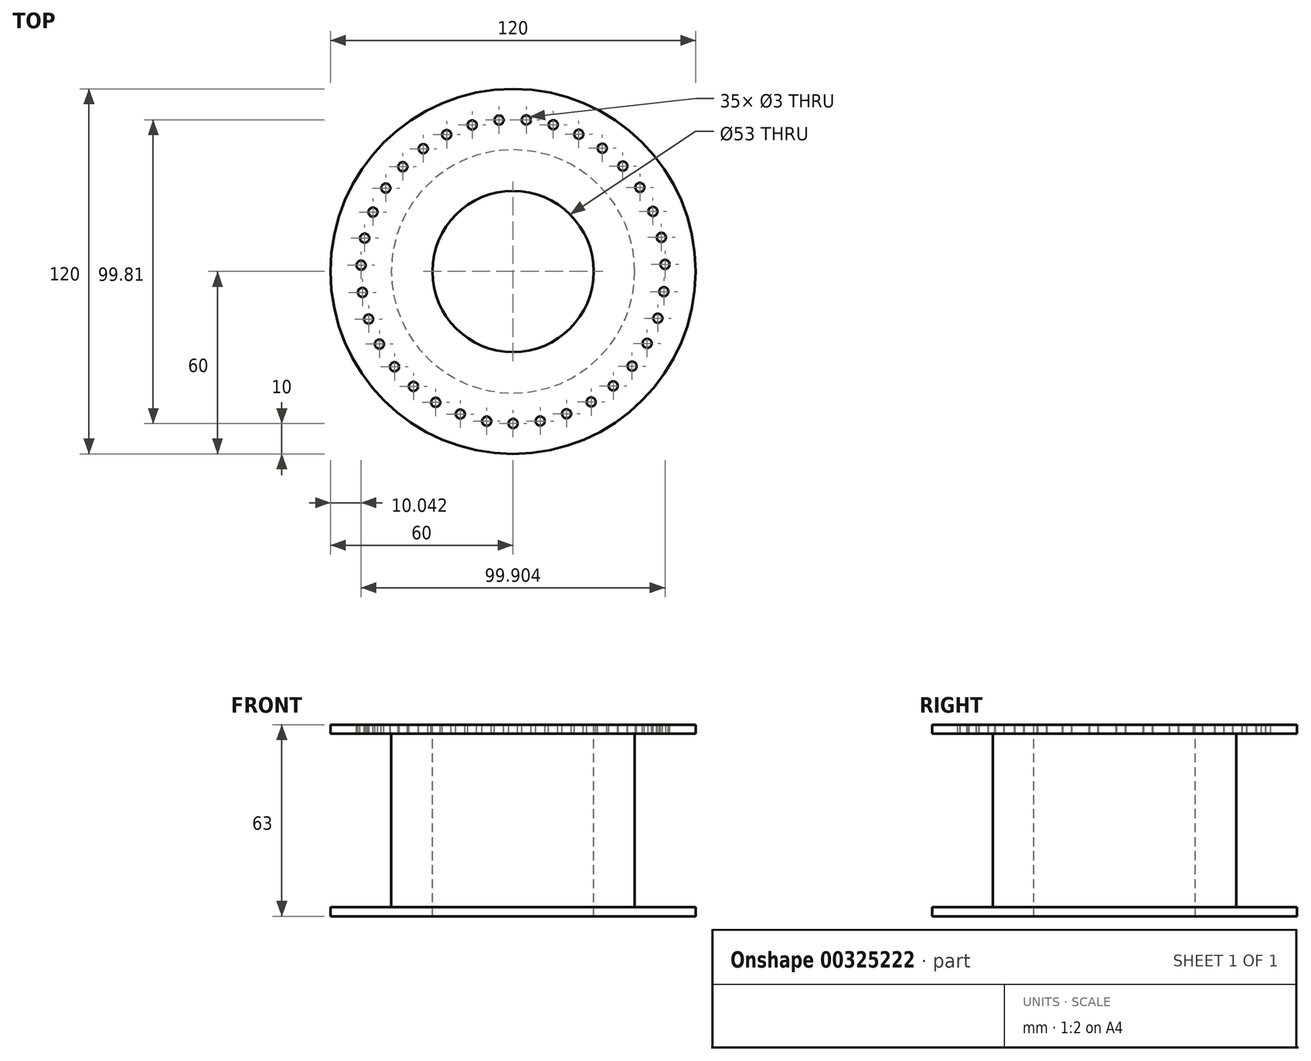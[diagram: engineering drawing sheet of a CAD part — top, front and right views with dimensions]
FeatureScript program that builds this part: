
annotation { "Feature Type Name" : "Feature", "Feature Type Description" : "" }
export const myFeature = defineFeature(function(context is Context, id is Id, definition is map)
    precondition{}
    {
        {
            var Q0;
            Q0=qCreatedBy(makeId("Top.planeOp"),FACE);
            var sketch = newSketch(context, id + "F0", { "sketchPlane" : qUnion([Q0])});
            skCircle(sketch, "E0", {"center": v(0, 0) * mm, "radius": 60 * mm});
            skSolve(sketch);
        }
        {
            var Q0;
            Q0=makeQuery(id+"F0.imprint","IMPRINT",FACE,{"disambiguationData":[TD([[makeQuery(id+"F0.imprint","IMPRINT",EDGE,{"derivedFrom":sQuery(id+"F0.wireOp",EDGE,"E0")}),1.0]])]});
            extrude(context, id + "F1", {"entities" : qUnion([Q0]), "depth" : 3 * mm});
        }
        {
            var Q0;
            Q0=makeQuery(id+"F1.opExtrude","CAP_FACE",FACE,{"disambiguationData":[OSD([sQuery(id+"F0.wireOp",EDGE,"E0")])],"isStart":false});
            var sketch = newSketch(context, id + "F2", { "sketchPlane" : qUnion([Q0])});
            skCircle(sketch, "E1", {"center": v(0, 0) * mm, "radius": 40 * mm});
            skSolve(sketch);
        }
        {
            var Q0;
            Q0=makeQuery(id+"F2.imprint","IMPRINT",FACE,{"disambiguationData":[TD([[makeQuery(id+"F2.imprint","IMPRINT",EDGE,{"derivedFrom":sQuery(id+"F2.wireOp",EDGE,"E1")}),1.0]])]});
            extrude(context, id + "F3", {"entities" : qUnion([Q0]), "operationType" : NewBodyOperationType.ADD, "depth" : 57 * mm});
        }
        {
            var Q0;
            Q0=makeQuery(id+"F3.opExtrude","CAP_FACE",FACE,{"disambiguationData":[OSD([sQuery(id+"F2.wireOp",EDGE,"E1")])],"isStart":false});
            var sketch = newSketch(context, id + "F4", { "sketchPlane" : qUnion([Q0])});
            skCircle(sketch, "E2", {"center": v(0, 0) * mm, "radius": 60 * mm});
            skSolve(sketch);
        }
        {
            var Q0;
            Q0=makeQuery(id+"F4.imprint","IMPRINT",FACE,{"disambiguationData":[TD([[makeQuery(id+"F4.imprint","IMPRINT",EDGE,{"derivedFrom":sQuery(id+"F4.wireOp",EDGE,"E2")}),1.0]])]});
            var Q1;
            Q1=makeQuery(id+"F4.imprint","IMPRINT",FACE,{"disambiguationData":[TD([[makeQuery(id+"F4.imprint","IMPRINT",EDGE,{"derivedFrom":makeQuery(id+"F3.opExtrude","CAP_EDGE",EDGE,{"disambiguationData":[OSD([sQuery(id+"F2.wireOp",EDGE,"E1")])],"isStart":false})}),1.0]])]});
            extrude(context, id + "F5", {"entities" : qUnion([Q0, Q1]), "operationType" : NewBodyOperationType.ADD, "depth" : 3 * mm});
        }
        {
            var Q0;
            Q0=makeQuery(id+"F5.opExtrude","CAP_FACE",FACE,{"disambiguationData":[OSD([sQuery(id+"F4.wireOp",EDGE,"E2")])],"isStart":false});
            var sketch = newSketch(context, id + "F6", { "sketchPlane" : qUnion([Q0])});
            skCircle(sketch, "E3", {"center": v(0, 0) * mm, "radius": 26.5 * mm});
            skSolve(sketch);
        }
        {
            var Q0;
            Q0=makeQuery(id+"F6.imprint","IMPRINT",FACE,{"disambiguationData":[TD([[makeQuery(id+"F6.imprint","IMPRINT",EDGE,{"derivedFrom":sQuery(id+"F6.wireOp",EDGE,"E3")}),1.0]])]});
            extrude(context, id + "F7", {"entities" : qUnion([Q0]), "operationType" : NewBodyOperationType.REMOVE, "oppositeDirection" : true, "depth" : 63 * mm});
        }
        {
            var Q0;
            Q0=makeQuery(id+"F5.opExtrude","CAP_FACE",FACE,{"disambiguationData":[OSD([sQuery(id+"F4.wireOp",EDGE,"E2")])],"isStart":false});
            var sketch = newSketch(context, id + "F8", { "sketchPlane" : qUnion([Q0])});
            skCircle(sketch, "E4", {"center": v(0, -50) * mm, "radius": 1.5 * mm});
            skCircle(sketch, "E5.1.0", {"center": v(8.94, -49.2) * mm, "radius": 1.5 * mm});
            skCircle(sketch, "E5.2.0", {"center": v(17.58, -46.8) * mm, "radius": 1.5 * mm});
            skCircle(sketch, "E5.3.0", {"center": v(25.66, -42.91) * mm, "radius": 1.5 * mm});
            skCircle(sketch, "E5.4.0", {"center": v(32.92, -37.63) * mm, "radius": 1.5 * mm});
            skCircle(sketch, "E5.5.0", {"center": v(39.11, -31.15) * mm, "radius": 1.5 * mm});
            skCircle(sketch, "E5.6.0", {"center": v(44.05, -23.65) * mm, "radius": 1.5 * mm});
            skCircle(sketch, "E5.7.0", {"center": v(47.57, -15.4) * mm, "radius": 1.5 * mm});
            skCircle(sketch, "E5.8.0", {"center": v(49.56, -6.65) * mm, "radius": 1.5 * mm});
            skCircle(sketch, "E5.9.0", {"center": v(49.95, 2.3) * mm, "radius": 1.5 * mm});
            skCircle(sketch, "E5.10.0", {"center": v(48.73, 11.2) * mm, "radius": 1.5 * mm});
            skCircle(sketch, "E5.11.0", {"center": v(45.94, 19.73) * mm, "radius": 1.5 * mm});
            skCircle(sketch, "E5.12.0", {"center": v(41.68, 27.62) * mm, "radius": 1.5 * mm});
            skCircle(sketch, "E5.13.0", {"center": v(36.07, 34.62) * mm, "radius": 1.5 * mm});
            skCircle(sketch, "E5.14.0", {"center": v(29.3, 40.51) * mm, "radius": 1.5 * mm});
            skCircle(sketch, "E5.15.0", {"center": v(21.6, 45.1) * mm, "radius": 1.5 * mm});
            skCircle(sketch, "E5.16.0", {"center": v(13.19, 48.23) * mm, "radius": 1.5 * mm});
            skCircle(sketch, "E5.17.0", {"center": v(4.36, 49.8) * mm, "radius": 1.5 * mm});
            skCircle(sketch, "E5.18.0", {"center": v(-4.61, 49.79) * mm, "radius": 1.5 * mm});
            skCircle(sketch, "E5.19.0", {"center": v(-13.44, 48.16) * mm, "radius": 1.5 * mm});
            skCircle(sketch, "E5.20.0", {"center": v(-21.83, 44.98) * mm, "radius": 1.5 * mm});
            skCircle(sketch, "E5.21.0", {"center": v(-29.51, 40.36) * mm, "radius": 1.5 * mm});
            skCircle(sketch, "E5.22.0", {"center": v(-36.25, 34.44) * mm, "radius": 1.5 * mm});
            skCircle(sketch, "E5.23.0", {"center": v(-41.82, 27.4) * mm, "radius": 1.5 * mm});
            skCircle(sketch, "E5.24.0", {"center": v(-46.05, 19.49) * mm, "radius": 1.5 * mm});
            skCircle(sketch, "E5.25.0", {"center": v(-48.79, 10.95) * mm, "radius": 1.5 * mm});
            skCircle(sketch, "E5.26.0", {"center": v(-49.96, 2.05) * mm, "radius": 1.5 * mm});
            skCircle(sketch, "E5.27.0", {"center": v(-49.52, -6.9) * mm, "radius": 1.5 * mm});
            skCircle(sketch, "E5.28.0", {"center": v(-47.49, -15.65) * mm, "radius": 1.5 * mm});
            skCircle(sketch, "E5.29.0", {"center": v(-43.93, -23.88) * mm, "radius": 1.5 * mm});
            skCircle(sketch, "E5.30.0", {"center": v(-38.95, -31.35) * mm, "radius": 1.5 * mm});
            skCircle(sketch, "E5.31.0", {"center": v(-32.73, -37.8) * mm, "radius": 1.5 * mm});
            skCircle(sketch, "E5.32.0", {"center": v(-25.44, -43.04) * mm, "radius": 1.5 * mm});
            skCircle(sketch, "E5.33.0", {"center": v(-17.34, -46.9) * mm, "radius": 1.5 * mm});
            skCircle(sketch, "E5.34.0", {"center": v(-8.68, -49.24) * mm, "radius": 1.5 * mm});
            skPoint(sketch, "E5.center", {"position": v(0, 0) * mm});
            skLineSegment(sketch, "E5.anchor1", {"start": v(0, 0) * mm, "end": v(0, -50) * mm, "construction": true});
            skLineSegment(sketch, "E5.anchor2", {"start": v(0, 0) * mm, "end": v(-8.68, -49.24) * mm, "construction": true});
            skSolve(sketch);
        }
        {
            var Q0;
            Q0=makeQuery(id+"F8.imprint","IMPRINT",FACE,{"disambiguationData":[TD([[makeQuery(id+"F8.imprint","IMPRINT",EDGE,{"derivedFrom":sQuery(id+"F8.wireOp",EDGE,"E5.27.0")}),1.0]])]});
            var Q1;
            Q1=makeQuery(id+"F8.imprint","IMPRINT",FACE,{"disambiguationData":[TD([[makeQuery(id+"F8.imprint","IMPRINT",EDGE,{"derivedFrom":sQuery(id+"F8.wireOp",EDGE,"E5.26.0")}),1.0]])]});
            var Q2;
            Q2=makeQuery(id+"F8.imprint","IMPRINT",FACE,{"disambiguationData":[TD([[makeQuery(id+"F8.imprint","IMPRINT",EDGE,{"derivedFrom":sQuery(id+"F8.wireOp",EDGE,"E5.25.0")}),1.0]])]});
            var Q3;
            Q3=makeQuery(id+"F8.imprint","IMPRINT",FACE,{"disambiguationData":[TD([[makeQuery(id+"F8.imprint","IMPRINT",EDGE,{"derivedFrom":sQuery(id+"F8.wireOp",EDGE,"E5.28.0")}),1.0]])]});
            var Q4;
            Q4=makeQuery(id+"F8.imprint","IMPRINT",FACE,{"disambiguationData":[TD([[makeQuery(id+"F8.imprint","IMPRINT",EDGE,{"derivedFrom":sQuery(id+"F8.wireOp",EDGE,"E5.29.0")}),1.0]])]});
            var Q5;
            Q5=makeQuery(id+"F8.imprint","IMPRINT",FACE,{"disambiguationData":[TD([[makeQuery(id+"F8.imprint","IMPRINT",EDGE,{"derivedFrom":sQuery(id+"F8.wireOp",EDGE,"E5.30.0")}),1.0]])]});
            var Q6;
            Q6=makeQuery(id+"F8.imprint","IMPRINT",FACE,{"disambiguationData":[TD([[makeQuery(id+"F8.imprint","IMPRINT",EDGE,{"derivedFrom":sQuery(id+"F8.wireOp",EDGE,"E5.31.0")}),1.0]])]});
            var Q7;
            Q7=makeQuery(id+"F8.imprint","IMPRINT",FACE,{"disambiguationData":[TD([[makeQuery(id+"F8.imprint","IMPRINT",EDGE,{"derivedFrom":sQuery(id+"F8.wireOp",EDGE,"E5.32.0")}),1.0]])]});
            var Q8;
            Q8=makeQuery(id+"F8.imprint","IMPRINT",FACE,{"disambiguationData":[TD([[makeQuery(id+"F8.imprint","IMPRINT",EDGE,{"derivedFrom":sQuery(id+"F8.wireOp",EDGE,"E5.33.0")}),1.0]])]});
            var Q9;
            Q9=makeQuery(id+"F8.imprint","IMPRINT",FACE,{"disambiguationData":[TD([[makeQuery(id+"F8.imprint","IMPRINT",EDGE,{"derivedFrom":sQuery(id+"F8.wireOp",EDGE,"E5.34.0")}),1.0]])]});
            var Q10;
            Q10=makeQuery(id+"F8.imprint","IMPRINT",FACE,{"disambiguationData":[TD([[makeQuery(id+"F8.imprint","IMPRINT",EDGE,{"derivedFrom":sQuery(id+"F8.wireOp",EDGE,"E4")}),1.0]])]});
            var Q11;
            Q11=makeQuery(id+"F8.imprint","IMPRINT",FACE,{"disambiguationData":[TD([[makeQuery(id+"F8.imprint","IMPRINT",EDGE,{"derivedFrom":sQuery(id+"F8.wireOp",EDGE,"E5.1.0")}),1.0]])]});
            var Q12;
            Q12=makeQuery(id+"F8.imprint","IMPRINT",FACE,{"disambiguationData":[TD([[makeQuery(id+"F8.imprint","IMPRINT",EDGE,{"derivedFrom":sQuery(id+"F8.wireOp",EDGE,"E5.2.0")}),1.0]])]});
            var Q13;
            Q13=makeQuery(id+"F8.imprint","IMPRINT",FACE,{"disambiguationData":[TD([[makeQuery(id+"F8.imprint","IMPRINT",EDGE,{"derivedFrom":sQuery(id+"F8.wireOp",EDGE,"E5.3.0")}),1.0]])]});
            var Q14;
            Q14=makeQuery(id+"F8.imprint","IMPRINT",FACE,{"disambiguationData":[TD([[makeQuery(id+"F8.imprint","IMPRINT",EDGE,{"derivedFrom":sQuery(id+"F8.wireOp",EDGE,"E5.4.0")}),1.0]])]});
            var Q15;
            Q15=makeQuery(id+"F8.imprint","IMPRINT",FACE,{"disambiguationData":[TD([[makeQuery(id+"F8.imprint","IMPRINT",EDGE,{"derivedFrom":sQuery(id+"F8.wireOp",EDGE,"E5.6.0")}),1.0]])]});
            var Q16;
            Q16=makeQuery(id+"F8.imprint","IMPRINT",FACE,{"disambiguationData":[TD([[makeQuery(id+"F8.imprint","IMPRINT",EDGE,{"derivedFrom":sQuery(id+"F8.wireOp",EDGE,"E5.7.0")}),1.0]])]});
            var Q17;
            Q17=makeQuery(id+"F8.imprint","IMPRINT",FACE,{"disambiguationData":[TD([[makeQuery(id+"F8.imprint","IMPRINT",EDGE,{"derivedFrom":sQuery(id+"F8.wireOp",EDGE,"E5.8.0")}),1.0]])]});
            var Q18;
            Q18=makeQuery(id+"F8.imprint","IMPRINT",FACE,{"disambiguationData":[TD([[makeQuery(id+"F8.imprint","IMPRINT",EDGE,{"derivedFrom":sQuery(id+"F8.wireOp",EDGE,"E5.5.0")}),1.0]])]});
            var Q19;
            Q19=makeQuery(id+"F8.imprint","IMPRINT",FACE,{"disambiguationData":[TD([[makeQuery(id+"F8.imprint","IMPRINT",EDGE,{"derivedFrom":sQuery(id+"F8.wireOp",EDGE,"E5.9.0")}),1.0]])]});
            var Q20;
            Q20=makeQuery(id+"F8.imprint","IMPRINT",FACE,{"disambiguationData":[TD([[makeQuery(id+"F8.imprint","IMPRINT",EDGE,{"derivedFrom":sQuery(id+"F8.wireOp",EDGE,"E5.10.0")}),1.0]])]});
            var Q21;
            Q21=makeQuery(id+"F8.imprint","IMPRINT",FACE,{"disambiguationData":[TD([[makeQuery(id+"F8.imprint","IMPRINT",EDGE,{"derivedFrom":sQuery(id+"F8.wireOp",EDGE,"E5.11.0")}),1.0]])]});
            var Q22;
            Q22=makeQuery(id+"F8.imprint","IMPRINT",FACE,{"disambiguationData":[TD([[makeQuery(id+"F8.imprint","IMPRINT",EDGE,{"derivedFrom":sQuery(id+"F8.wireOp",EDGE,"E5.12.0")}),1.0]])]});
            var Q23;
            Q23=makeQuery(id+"F8.imprint","IMPRINT",FACE,{"disambiguationData":[TD([[makeQuery(id+"F8.imprint","IMPRINT",EDGE,{"derivedFrom":sQuery(id+"F8.wireOp",EDGE,"E5.13.0")}),1.0]])]});
            var Q24;
            Q24=makeQuery(id+"F8.imprint","IMPRINT",FACE,{"disambiguationData":[TD([[makeQuery(id+"F8.imprint","IMPRINT",EDGE,{"derivedFrom":sQuery(id+"F8.wireOp",EDGE,"E5.15.0")}),1.0]])]});
            var Q25;
            Q25=makeQuery(id+"F8.imprint","IMPRINT",FACE,{"disambiguationData":[TD([[makeQuery(id+"F8.imprint","IMPRINT",EDGE,{"derivedFrom":sQuery(id+"F8.wireOp",EDGE,"E5.14.0")}),1.0]])]});
            var Q26;
            Q26=makeQuery(id+"F8.imprint","IMPRINT",FACE,{"disambiguationData":[TD([[makeQuery(id+"F8.imprint","IMPRINT",EDGE,{"derivedFrom":sQuery(id+"F8.wireOp",EDGE,"E5.16.0")}),1.0]])]});
            var Q27;
            Q27=makeQuery(id+"F8.imprint","IMPRINT",FACE,{"disambiguationData":[TD([[makeQuery(id+"F8.imprint","IMPRINT",EDGE,{"derivedFrom":sQuery(id+"F8.wireOp",EDGE,"E5.19.0")}),1.0]])]});
            var Q28;
            Q28=makeQuery(id+"F8.imprint","IMPRINT",FACE,{"disambiguationData":[TD([[makeQuery(id+"F8.imprint","IMPRINT",EDGE,{"derivedFrom":sQuery(id+"F8.wireOp",EDGE,"E5.18.0")}),1.0]])]});
            var Q29;
            Q29=makeQuery(id+"F8.imprint","IMPRINT",FACE,{"disambiguationData":[TD([[makeQuery(id+"F8.imprint","IMPRINT",EDGE,{"derivedFrom":sQuery(id+"F8.wireOp",EDGE,"E5.17.0")}),1.0]])]});
            var Q30;
            Q30=makeQuery(id+"F8.imprint","IMPRINT",FACE,{"disambiguationData":[TD([[makeQuery(id+"F8.imprint","IMPRINT",EDGE,{"derivedFrom":sQuery(id+"F8.wireOp",EDGE,"E5.21.0")}),1.0]])]});
            var Q31;
            Q31=makeQuery(id+"F8.imprint","IMPRINT",FACE,{"disambiguationData":[TD([[makeQuery(id+"F8.imprint","IMPRINT",EDGE,{"derivedFrom":sQuery(id+"F8.wireOp",EDGE,"E5.20.0")}),1.0]])]});
            var Q32;
            Q32=makeQuery(id+"F8.imprint","IMPRINT",FACE,{"disambiguationData":[TD([[makeQuery(id+"F8.imprint","IMPRINT",EDGE,{"derivedFrom":sQuery(id+"F8.wireOp",EDGE,"E5.22.0")}),1.0]])]});
            var Q33;
            Q33=makeQuery(id+"F8.imprint","IMPRINT",FACE,{"disambiguationData":[TD([[makeQuery(id+"F8.imprint","IMPRINT",EDGE,{"derivedFrom":sQuery(id+"F8.wireOp",EDGE,"E5.23.0")}),1.0]])]});
            var Q34;
            Q34=makeQuery(id+"F8.imprint","IMPRINT",FACE,{"disambiguationData":[TD([[makeQuery(id+"F8.imprint","IMPRINT",EDGE,{"derivedFrom":sQuery(id+"F8.wireOp",EDGE,"E5.24.0")}),1.0]])]});
            extrude(context, id + "F9", {"entities" : qUnion([Q0, Q1, Q2, Q3, Q4, Q5, Q6, Q7, Q8, Q9, Q10, Q11, Q12, Q13, Q14, Q15, Q16, Q17, Q18, Q19, Q20, Q21, Q22, Q23, Q24, Q25, Q26, Q27, Q28, Q29, Q30, Q31, Q32, Q33, Q34]), "operationType" : NewBodyOperationType.REMOVE, "oppositeDirection" : true, "depth" : 25 * mm});
        }
    });
